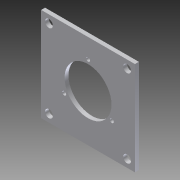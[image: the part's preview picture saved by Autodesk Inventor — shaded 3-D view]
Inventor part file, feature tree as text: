
AUTODESK INVENTOR PART (.ipt)
format: ipt  version: 2012 (Build 160160000, 160)  size: 108,544 bytes
history: native  units: in
note: dims shown in document units (in); Inventor stores cm internally (conversion verified against a paired STEP export)
features: sketch x2, hole x2, extrude x1
ambient origin geometry x8: Origin, YZ Plane, XZ Plane, XY Plane, X Axis, Y Axis, Z Axis, Center Point
bodies: Solid1 (feature_tree)
feature tree (5):
  sketch  "Sketch1"  dims[d0=3.0in d1=3.0in]
  extrude  "Extrusion1"  Depth=3.0in
  hole  "Hole1"  [1 undecoded]
  hole  "Hole2"  [1 undecoded]
  sketch  "Sketch2"  dims[d2=1.5in d3=1.5in d4=1.5in d5=0.25in d6=0.25in d7=0.25in d8=0.25in d10=0.125in d11=0.0in d12=0.25in d13=0.75in d14=0.375in d15=0.25in d16=0.5635in d17=1.0in d18=0.8108in d19=1.523in d20=1.523in d21=1.523in d22=1.7586in d24=1.5in d25=0.125in d26=0.75in d27=0.375in d28=0.25in d29=0.5635in d30=1.0in d31=0.8108in]
note: 2 required parameter values undecoded (feature->parameter linkage not recoverable at this tier; creation-order binding heuristic only, values carry confidence <= 0.55)
